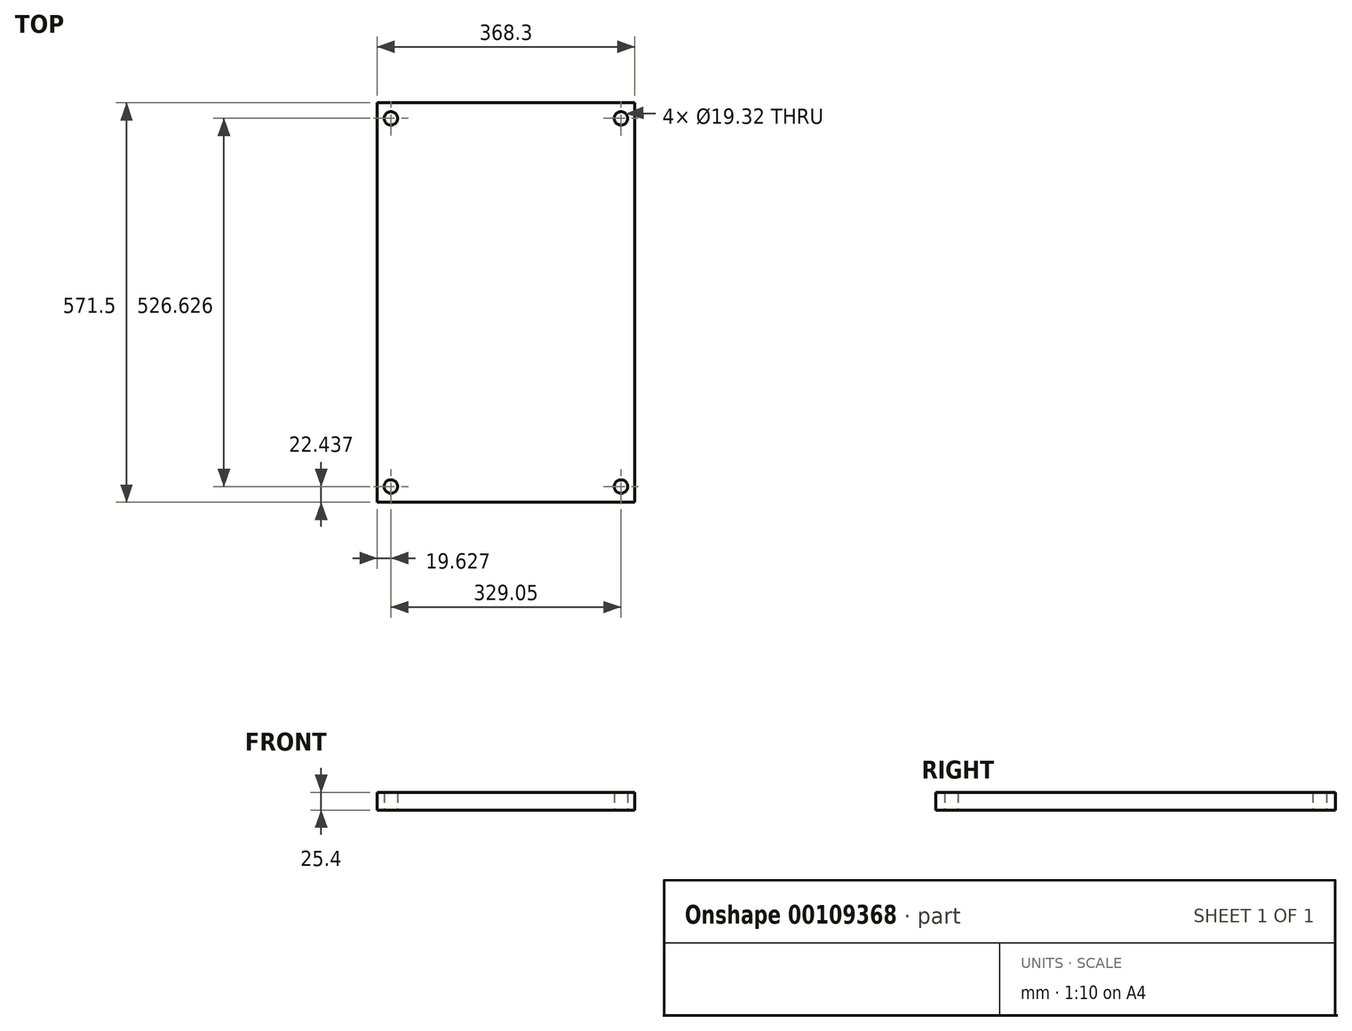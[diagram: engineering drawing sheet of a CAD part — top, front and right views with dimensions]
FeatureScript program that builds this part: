
annotation { "Feature Type Name" : "Feature", "Feature Type Description" : "" }
export const myFeature = defineFeature(function(context is Context, id is Id, definition is map)
    precondition{}
    {
        {
            var Q0;
            Q0=qCreatedBy(makeId("Top.planeOp"),FACE);
            var sketch = newSketch(context, id + "F0", { "sketchPlane" : qUnion([Q0])});
            skLineSegment(sketch, "E0.bottom", {"start": v(-202.28, 314.66) * mm, "end": v(166.02, 314.66) * mm});
            skLineSegment(sketch, "E0.top", {"start": v(-202.28, -256.84) * mm, "end": v(166.02, -256.84) * mm});
            skLineSegment(sketch, "E0.left", {"start": v(-202.28, 314.66) * mm, "end": v(-202.28, -256.84) * mm});
            skLineSegment(sketch, "E0.right", {"start": v(166.02, 314.66) * mm, "end": v(166.02, -256.84) * mm});
            skSolve(sketch);
        }
        {
            var Q0;
            Q0=makeQuery(id+"F0.imprint","IMPRINT",FACE,{"disambiguationData":[TD([[makeQuery(id+"F0.imprint","IMPRINT",EDGE,{"derivedFrom":sQuery(id+"F0.wireOp",EDGE,"E0.bottom")}),-1.0]])]});
            extrude(context, id + "F1", {"entities" : qUnion([Q0]), "depth" : 25.4 * mm});
        }
        {
            var Q0;
            Q0=makeQuery(id+"F1.opExtrude","CAP_FACE",FACE,{"disambiguationData":[OSD([sQuery(id+"F0.wireOp",EDGE,"E0.bottom"),sQuery(id+"F0.wireOp",EDGE,"E0.top"),sQuery(id+"F0.wireOp",EDGE,"E0.left"),sQuery(id+"F0.wireOp",EDGE,"E0.right")])],"isStart":true});
            var sketch = newSketch(context, id + "F2", { "sketchPlane" : qUnion([Q0])});
            skCircle(sketch, "E1", {"center": v(-182.65, 234.4) * mm, "radius": 9.66 * mm});
            skCircle(sketch, "E2.MirrorC", {"center": v(146.4, 234.4) * mm, "radius": 9.66 * mm});
            skPoint(sketch, "E3.endSnap0", {"position": v(-202.28, -28.91) * mm});
            skCircle(sketch, "E4.MirrorC", {"center": v(-182.65, -292.22) * mm, "radius": 9.66 * mm});
            skCircle(sketch, "E5.MirrorC", {"center": v(146.4, -292.22) * mm, "radius": 9.66 * mm});
            skSolve(sketch);
        }
        {
            var Q0;
            Q0 = qSketchRegion(id + "F2", true);
            extrude(context, id + "F3", {"entities" : qUnion([Q0]), "operationType" : NewBodyOperationType.REMOVE, "oppositeDirection" : true, "depth" : 25.4 * mm});
        }
    });
